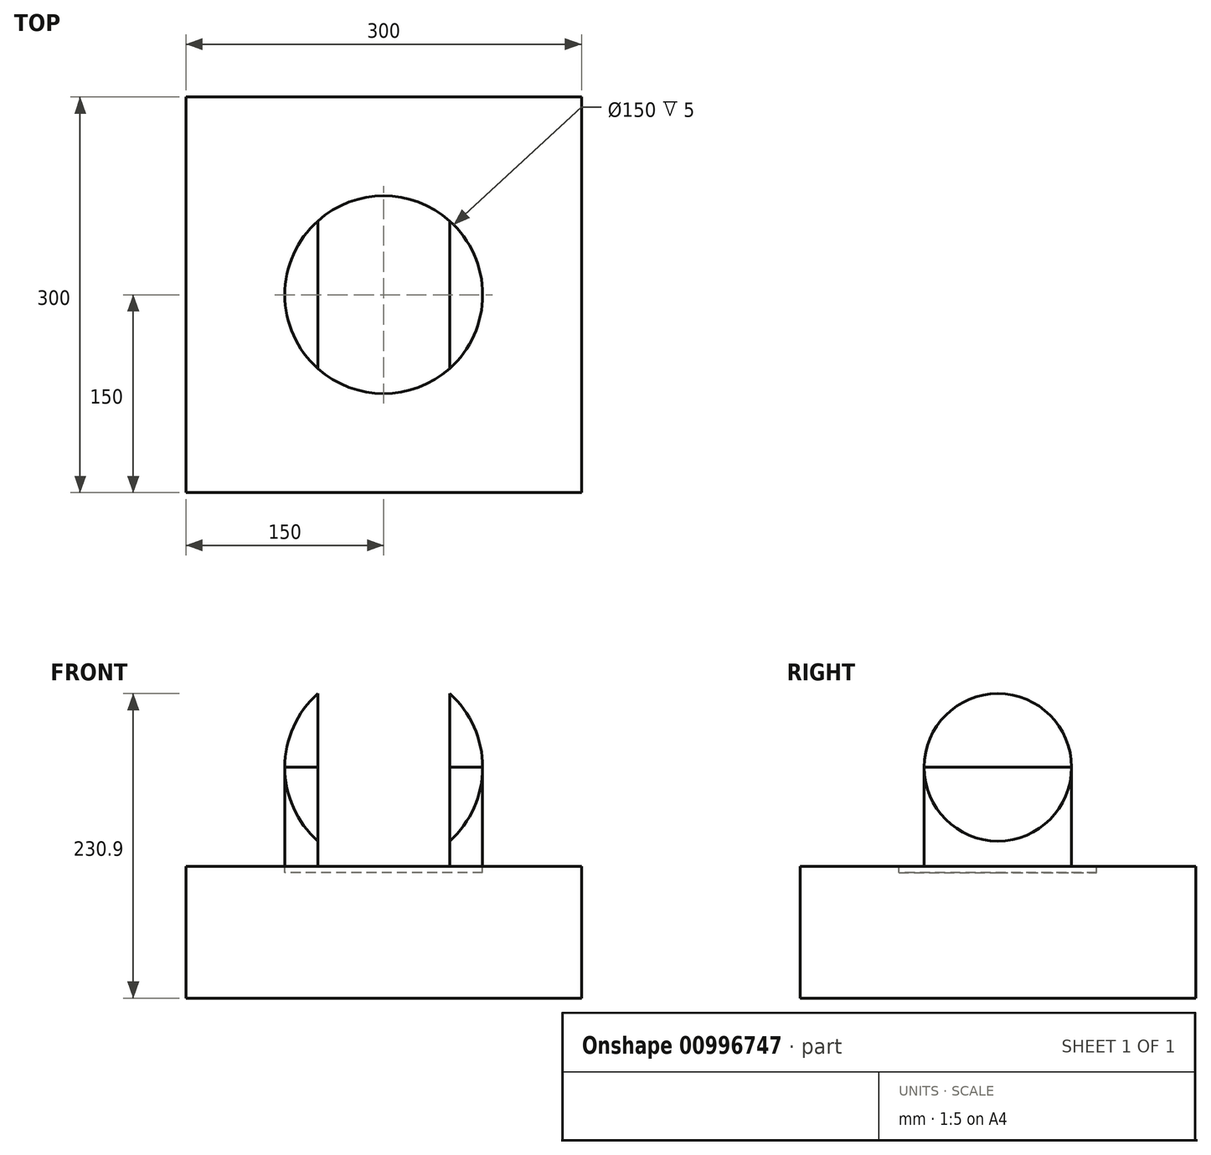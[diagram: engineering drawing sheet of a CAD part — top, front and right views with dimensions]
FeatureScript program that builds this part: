
annotation { "Feature Type Name" : "Feature", "Feature Type Description" : "" }
export const myFeature = defineFeature(function(context is Context, id is Id, definition is map)
    precondition{}
    {
        {
            var Q0;
            Q0=qCreatedBy(makeId("Top.planeOp"),FACE);
            var sketch = newSketch(context, id + "F0", { "sketchPlane" : qUnion([Q0])});
            skLineSegment(sketch, "E0.bottom", {"start": v(-150, 150) * mm, "end": v(150, 150) * mm});
            skLineSegment(sketch, "E0.top", {"start": v(-150, -150) * mm, "end": v(150, -150) * mm});
            skLineSegment(sketch, "E0.left", {"start": v(-150, 150) * mm, "end": v(-150, -150) * mm});
            skLineSegment(sketch, "E0.right", {"start": v(150, 150) * mm, "end": v(150, -150) * mm});
            skPoint(sketch, "E0.middle", {"position": v(0, 0) * mm});
            skSolve(sketch);
        }
        {
            var Q0;
            Q0 = qSketchRegion(id + "F0", true);
            extrude(context, id + "F1", {"entities" : qUnion([Q0]), "oppositeDirection" : true, "depth" : 100 * mm, "offsetDistance" : 25 * mm});
        }
        {
            var Q0;
            Q0=makeQuery(id+"F1.opExtrude","CAP_FACE",FACE,{"disambiguationData":[OSD([sQuery(id+"F0.wireOp",EDGE,"E0.bottom"),sQuery(id+"F0.wireOp",EDGE,"E0.top"),sQuery(id+"F0.wireOp",EDGE,"E0.left"),sQuery(id+"F0.wireOp",EDGE,"E0.right")])],"isStart":true});
            var sketch = newSketch(context, id + "F2", { "sketchPlane" : qUnion([Q0])});
            skCircle(sketch, "E1", {"center": v(0, 0) * mm, "radius": 75 * mm});
            skSolve(sketch);
        }
        {
            var Q0;
            Q0 = qSketchRegion(id + "F2", true);
            extrude(context, id + "F3", {"entities" : qUnion([Q0]), "oppositeDirection" : true, "depth" : 5 * mm, "offsetDistance" : 25 * mm});
        }
        {
            var Q0;
            Q0=makeQuery(id+"F3.opExtrude","SWEPT_BODY",BODY,{"disambiguationData":[OSD([sQuery(id+"F2.wireOp",EDGE,"E1")])]});
            var Q1;
            Q1=makeQuery(id+"F1.opExtrude","SWEPT_BODY",BODY,{"disambiguationData":[OSD([sQuery(id+"F0.wireOp",EDGE,"E0.bottom"),sQuery(id+"F0.wireOp",EDGE,"E0.top"),sQuery(id+"F0.wireOp",EDGE,"E0.left"),sQuery(id+"F0.wireOp",EDGE,"E0.right")])]});
            booleanBodies(context, id + "F4", {"operationType" : BooleanOperationType.SUBTRACTION, "tools" : qUnion([Q0]), "targets" : qUnion([Q1]), "keepTools" : true});
        }
        {
            var Q0;
            Q0=qCreatedBy(makeId("Front.planeOp"),FACE);
            var sketch = newSketch(context, id + "F5", { "sketchPlane" : qUnion([Q0])});
            skLineSegment(sketch, "E2", {"start": v(0, 0) * mm, "end": v(0, 75) * mm, "construction": true});
            skArc(sketch, "E3", {"start": v(0, 0) * mm, "mid": v(75, 75) * mm, "end": v(0, 150) * mm});
            skLineSegment(sketch, "E4", {"start": v(0, 150) * mm, "end": v(0, 0) * mm});
            skSolve(sketch);
        }
        {
            var Q0;
            Q0 = qSketchRegion(id + "F5", true);
            var Q1;
            Q1=sQuery(id+"F5.wireOp",EDGE,"E4");
            revolve(context, id + "F6", {"surfaceOperationType" : NewSurfaceOperationType.NEW, "entities" : qUnion([Q0]), "axis" : qUnion([Q1]), "revolveType" : RevolveType.FULL});
        }
        {
            var Q0;
            Q0=makeQuery(id+"F3.opExtrude","CAP_FACE",FACE,{"disambiguationData":[OSD([sQuery(id+"F2.wireOp",EDGE,"E1")])],"isStart":true});
            var sketch = newSketch(context, id + "F7", { "sketchPlane" : qUnion([Q0])});
            skArc(sketch, "E5", {"start": v(-75, 0) * mm, "mid": v(-68.47, 30.62) * mm, "end": v(-50, 55.9) * mm});
            skLineSegment(sketch, "E6", {"start": v(0, 0) * mm, "end": v(-75, 0) * mm, "construction": true});
            skLineSegment(sketch, "E7", {"start": v(-75, 0) * mm, "end": v(-50, 0) * mm, "construction": true});
            skLineSegment(sketch, "E8", {"start": v(-50, 0) * mm, "end": v(-50, 55.9) * mm});
            skLineSegment(sketch, "E9", {"start": v(0, 0) * mm, "end": v(0, 75) * mm, "construction": true});
            skLineSegment(sketch, "E10.MirrorCS", {"start": v(-50, 0) * mm, "end": v(-50, -55.9) * mm});
            skArc(sketch, "E11.MirrorCS", {"start": v(-75, 0) * mm, "mid": v(-68.47, -30.62) * mm, "end": v(-50, -55.9) * mm});
            skLineSegment(sketch, "E12.MirrorCS", {"start": v(50, 0) * mm, "end": v(50, 55.9) * mm});
            skLineSegment(sketch, "E13.MirrorCS", {"start": v(50, 0) * mm, "end": v(50, -55.9) * mm});
            skArc(sketch, "E14.MirrorCS", {"start": v(75, 0) * mm, "mid": v(68.47, -30.62) * mm, "end": v(50, -55.9) * mm});
            skArc(sketch, "E15.MirrorCS", {"start": v(75, 0) * mm, "mid": v(68.47, 30.62) * mm, "end": v(50, 55.9) * mm});
            skSolve(sketch);
        }
        {
            var Q0;
            Q0 = qSketchRegion(id + "F7", true);
            extrude(context, id + "F8", {"entities" : qUnion([Q0]), "endBound" : BoundingType.THROUGH_ALL, "depth" : 75 * mm, "offsetDistance" : 25 * mm});
        }
        {
            var Q0;
            Q0=makeQuery(id+"F8.opExtrude","SWEPT_BODY",BODY,{"disambiguationData":[OSD([sQuery(id+"F7.wireOp",EDGE,"E5"),sQuery(id+"F7.wireOp",EDGE,"E8"),sQuery(id+"F7.wireOp",EDGE,"E10.MirrorCS"),sQuery(id+"F7.wireOp",EDGE,"E11.MirrorCS")])]});
            var Q1;
            Q1=makeQuery(id+"F6.opRevolve","SWEPT_BODY",BODY,{"disambiguationData":[OSD([sQuery(id+"F5.wireOp",EDGE,"E3"),sQuery(id+"F5.wireOp",EDGE,"E4")])]});
            booleanBodies(context, id + "F9", {"operationType" : BooleanOperationType.INTERSECTION, "tools" : qUnion([Q0, Q1]), "keepTools" : true});
        }
        {
            var Q0;
            Q0=makeQuery(id+"F8.opExtrude","SWEPT_BODY",BODY,{"disambiguationData":[OSD([sQuery(id+"F7.wireOp",EDGE,"E12.MirrorCS"),sQuery(id+"F7.wireOp",EDGE,"E13.MirrorCS"),sQuery(id+"F7.wireOp",EDGE,"E14.MirrorCS"),sQuery(id+"F7.wireOp",EDGE,"E15.MirrorCS")])]});
            var Q1;
            Q1=makeQuery(id+"F6.opRevolve","SWEPT_BODY",BODY,{"disambiguationData":[OSD([sQuery(id+"F5.wireOp",EDGE,"E3"),sQuery(id+"F5.wireOp",EDGE,"E4")])]});
            booleanBodies(context, id + "F10", {"operationType" : BooleanOperationType.INTERSECTION, "tools" : qUnion([Q0, Q1]), "keepTools" : true});
        }
        {
            var Q0;
            Q0 = qSketchRegion(id + "F7", true);
            extrude(context, id + "F11", {"entities" : qUnion([Q0]), "depth" : 75 * mm, "offsetDistance" : 25 * mm});
        }
        {
            var Q0;
            Q0=makeQuery(id+"F8.opExtrude","SWEPT_BODY",BODY,{"disambiguationData":[OSD([sQuery(id+"F7.wireOp",EDGE,"E12.MirrorCS"),sQuery(id+"F7.wireOp",EDGE,"E13.MirrorCS"),sQuery(id+"F7.wireOp",EDGE,"E14.MirrorCS"),sQuery(id+"F7.wireOp",EDGE,"E15.MirrorCS")])]});
            deleteBodies(context, id + "F12", {"entities" : qUnion([Q0])});
        }
        {
            var Q0;
            Q0=makeQuery(id+"F8.opExtrude","SWEPT_BODY",BODY,{"disambiguationData":[OSD([sQuery(id+"F7.wireOp",EDGE,"E5"),sQuery(id+"F7.wireOp",EDGE,"E8"),sQuery(id+"F7.wireOp",EDGE,"E10.MirrorCS"),sQuery(id+"F7.wireOp",EDGE,"E11.MirrorCS")])]});
            deleteBodies(context, id + "F13", {"entities" : qUnion([Q0])});
        }
        {
            var Q0;
            Q0=makeQuery(id+"F6.opRevolve","SWEPT_BODY",BODY,{"disambiguationData":[OSD([sQuery(id+"F5.wireOp",EDGE,"E3"),sQuery(id+"F5.wireOp",EDGE,"E4")])]});
            deleteBodies(context, id + "F14", {"entities" : qUnion([Q0])});
        }
    });
